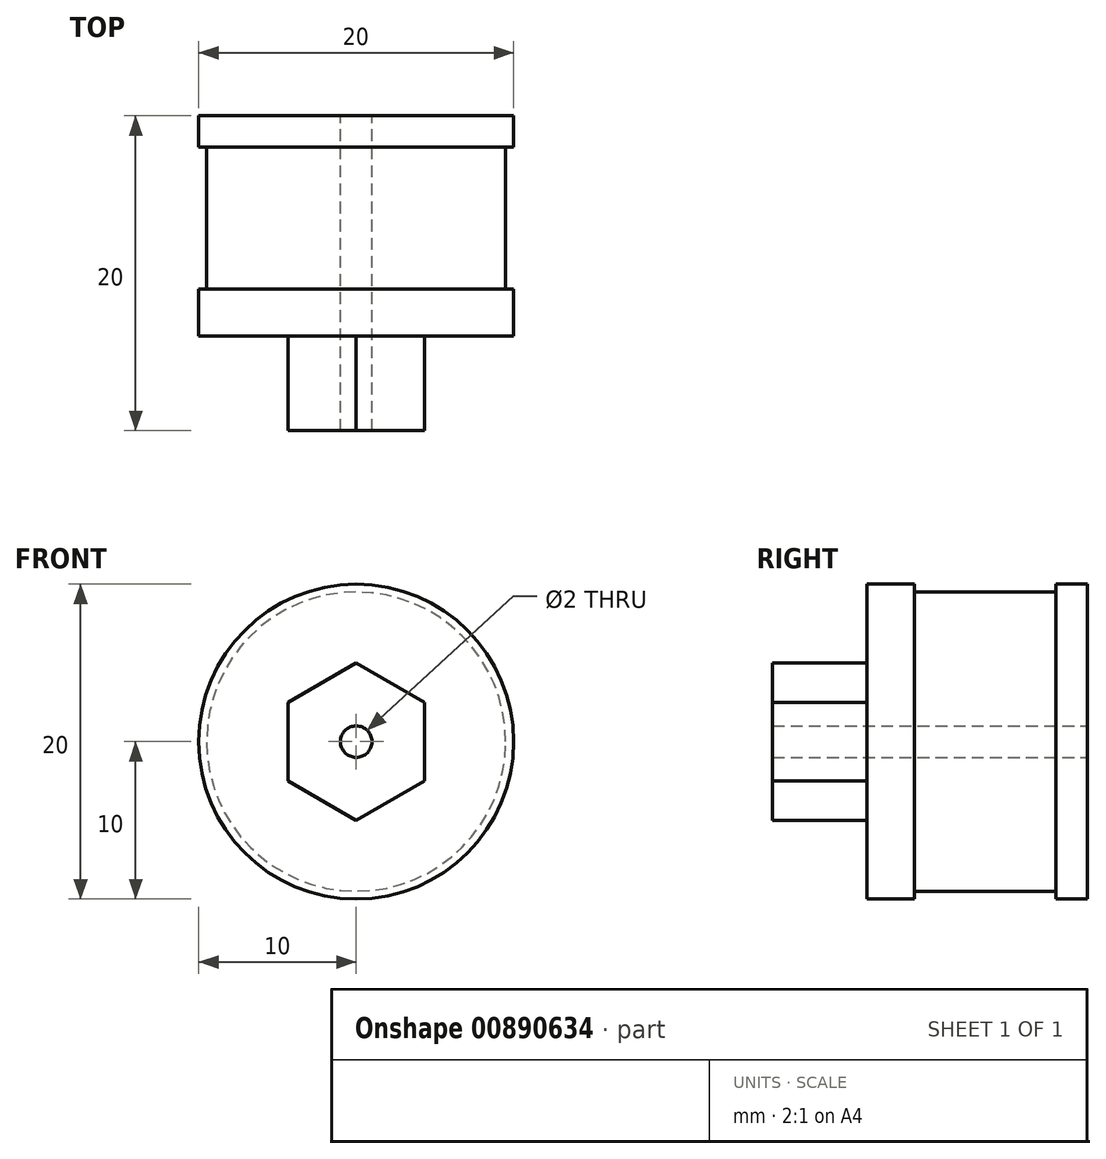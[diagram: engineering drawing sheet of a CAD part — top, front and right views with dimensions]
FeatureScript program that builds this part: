
annotation { "Feature Type Name" : "Feature", "Feature Type Description" : "" }
export const myFeature = defineFeature(function(context is Context, id is Id, definition is map)
    precondition{}
    {
        {
            var Q0;
            Q0=qCreatedBy(makeId("Front.planeOp"),FACE);
            var sketch = newSketch(context, id + "F0", { "sketchPlane" : qUnion([Q0])});
            skCircle(sketch, "E0", {"center": v(0, 0) * mm, "radius": 10 * mm});
            skCircle(sketch, "E1", {"center": v(0, 0) * mm, "radius": 5 * mm});
            skCircle(sketch, "E2", {"center": v(0, 0) * mm, "radius": 9.5 * mm});
            skCircle(sketch, "E3.cCircle", {"center": v(0, 0) * mm, "radius": 5 * mm, "construction": true});
            skLineSegment(sketch, "E3.0", {"start": v(0, 5) * mm, "end": v(4.33, 2.5) * mm});
            skLineSegment(sketch, "E3.1", {"start": v(4.33, 2.5) * mm, "end": v(4.33, -2.5) * mm});
            skLineSegment(sketch, "E3.2", {"start": v(4.33, -2.5) * mm, "end": v(0, -5) * mm});
            skLineSegment(sketch, "E3.3", {"start": v(0, -5) * mm, "end": v(-4.33, -2.5) * mm});
            skLineSegment(sketch, "E3.4", {"start": v(-4.33, -2.5) * mm, "end": v(-4.33, 2.5) * mm});
            skLineSegment(sketch, "E3.5", {"start": v(-4.33, 2.5) * mm, "end": v(0, 5) * mm});
            skCircle(sketch, "E4", {"center": v(0, 0) * mm, "radius": 1 * mm});
            skSolve(sketch);
        }
        {
            var Q0;
            Q0=makeQuery(id+"F0.imprint","IMPRINT",FACE,{"disambiguationData":[TD([[makeQuery(id+"F0.imprint","IMPRINT",EDGE,{"derivedFrom":sQuery(id+"F0.wireOp",EDGE,"E0")}),1.0]])]});
            var Q1;
            Q1=makeQuery(id+"F0.imprint","IMPRINT",FACE,{"disambiguationData":[TD([[makeQuery(id+"F0.imprint","IMPRINT",EDGE,{"derivedFrom":sQuery(id+"F0.wireOp",EDGE,"E2")}),1.0]])]});
            var Q2;
            {var subQ0=sQuery(id+"F0.wireOp",EDGE,"E3.0");Q2=makeQuery(id+"F0.imprint","IMPRINT",FACE,{"disambiguationData":[TD([[makeQuery(id+"F0.imprint","IMPRINT",EDGE,{"derivedFrom":subQ0}),1.0]])]});}
            var Q3;
            {var subQ0=sQuery(id+"F0.wireOp",EDGE,"E3.5");Q3=makeQuery(id+"F0.imprint","IMPRINT",FACE,{"disambiguationData":[TD([[makeQuery(id+"F0.imprint","IMPRINT",EDGE,{"derivedFrom":subQ0}),1.0]])]});}
            var Q4;
            {var subQ0=sQuery(id+"F0.wireOp",EDGE,"E3.4");Q4=makeQuery(id+"F0.imprint","IMPRINT",FACE,{"disambiguationData":[TD([[makeQuery(id+"F0.imprint","IMPRINT",EDGE,{"derivedFrom":subQ0}),1.0]])]});}
            var Q5;
            {var subQ0=sQuery(id+"F0.wireOp",EDGE,"E3.3");Q5=makeQuery(id+"F0.imprint","IMPRINT",FACE,{"disambiguationData":[TD([[makeQuery(id+"F0.imprint","IMPRINT",EDGE,{"derivedFrom":subQ0}),1.0]])]});}
            var Q6;
            {var subQ0=sQuery(id+"F0.wireOp",EDGE,"E3.2");Q6=makeQuery(id+"F0.imprint","IMPRINT",FACE,{"disambiguationData":[TD([[makeQuery(id+"F0.imprint","IMPRINT",EDGE,{"derivedFrom":subQ0}),1.0]])]});}
            var Q7;
            Q7=makeQuery(id+"F0.imprint","IMPRINT",FACE,{"disambiguationData":[TD([[makeQuery(id+"F0.imprint","IMPRINT",EDGE,{"derivedFrom":sQuery(id+"F0.wireOp",EDGE,"E3.0")}),-1.0]])]});
            var Q8;
            {var subQ0=sQuery(id+"F0.wireOp",EDGE,"E3.1");Q8=makeQuery(id+"F0.imprint","IMPRINT",FACE,{"disambiguationData":[TD([[makeQuery(id+"F0.imprint","IMPRINT",EDGE,{"derivedFrom":subQ0}),1.0]])]});}
            extrude(context, id + "F1", {"entities" : qUnion([Q0, Q1, Q2, Q3, Q4, Q5, Q6, Q7, Q8]), "depth" : 2 * mm, "offsetDistance" : 25 * mm});
        }
        {
            var Q0;
            {var subQ0=sQuery(id+"F0.wireOp",EDGE,"E3.5");Q0=makeQuery(id+"F0.imprint","IMPRINT",FACE,{"disambiguationData":[TD([[makeQuery(id+"F0.imprint","IMPRINT",EDGE,{"derivedFrom":subQ0}),1.0]])]});}
            var Q1;
            {var subQ0=sQuery(id+"F0.wireOp",EDGE,"E3.0");Q1=makeQuery(id+"F0.imprint","IMPRINT",FACE,{"disambiguationData":[TD([[makeQuery(id+"F0.imprint","IMPRINT",EDGE,{"derivedFrom":subQ0}),1.0]])]});}
            var Q2;
            Q2=makeQuery(id+"F0.imprint","IMPRINT",FACE,{"disambiguationData":[TD([[makeQuery(id+"F0.imprint","IMPRINT",EDGE,{"derivedFrom":sQuery(id+"F0.wireOp",EDGE,"E3.0")}),-1.0]])]});
            var Q3;
            {var subQ0=sQuery(id+"F0.wireOp",EDGE,"E3.1");Q3=makeQuery(id+"F0.imprint","IMPRINT",FACE,{"disambiguationData":[TD([[makeQuery(id+"F0.imprint","IMPRINT",EDGE,{"derivedFrom":subQ0}),1.0]])]});}
            var Q4;
            {var subQ0=sQuery(id+"F0.wireOp",EDGE,"E3.4");Q4=makeQuery(id+"F0.imprint","IMPRINT",FACE,{"disambiguationData":[TD([[makeQuery(id+"F0.imprint","IMPRINT",EDGE,{"derivedFrom":subQ0}),1.0]])]});}
            var Q5;
            {var subQ0=sQuery(id+"F0.wireOp",EDGE,"E3.3");Q5=makeQuery(id+"F0.imprint","IMPRINT",FACE,{"disambiguationData":[TD([[makeQuery(id+"F0.imprint","IMPRINT",EDGE,{"derivedFrom":subQ0}),1.0]])]});}
            var Q6;
            {var subQ0=sQuery(id+"F0.wireOp",EDGE,"E3.2");Q6=makeQuery(id+"F0.imprint","IMPRINT",FACE,{"disambiguationData":[TD([[makeQuery(id+"F0.imprint","IMPRINT",EDGE,{"derivedFrom":subQ0}),1.0]])]});}
            var Q7;
            Q7=makeQuery(id+"F0.imprint","IMPRINT",FACE,{"disambiguationData":[TD([[makeQuery(id+"F0.imprint","IMPRINT",EDGE,{"derivedFrom":sQuery(id+"F0.wireOp",EDGE,"E2")}),1.0]])]});
            extrude(context, id + "F2", {"entities" : qUnion([Q0, Q1, Q2, Q3, Q4, Q5, Q6, Q7]), "operationType" : NewBodyOperationType.ADD, "depth" : 12 * mm, "offsetDistance" : 25 * mm});
        }
        {
            var Q0;
            Q0=makeQuery(id+"F2.opExtrude","CAP_FACE",FACE,{"disambiguationData":[OSD([sQuery(id+"F0.wireOp",EDGE,"E2")])],"isStart":false});
            var sketch = newSketch(context, id + "F3", { "sketchPlane" : qUnion([Q0])});
            skCircle(sketch, "E5.0", {"center": v(0, 0) * mm, "radius": 10 * mm});
            skCircle(sketch, "E5.1", {"center": v(0, 0) * mm, "radius": 9.5 * mm});
            skCircle(sketch, "E5.2", {"center": v(0, 0) * mm, "radius": 5 * mm});
            skLineSegment(sketch, "E5.3", {"start": v(0, 5) * mm, "end": v(4.33, 2.5) * mm});
            skLineSegment(sketch, "E5.4", {"start": v(-4.33, 2.5) * mm, "end": v(0, 5) * mm});
            skLineSegment(sketch, "E5.5", {"start": v(0, -5) * mm, "end": v(-4.33, -2.5) * mm});
            skLineSegment(sketch, "E5.6", {"start": v(-4.33, -2.5) * mm, "end": v(-4.33, 2.5) * mm});
            skLineSegment(sketch, "E5.7", {"start": v(4.33, -2.5) * mm, "end": v(0, -5) * mm});
            skLineSegment(sketch, "E5.8", {"start": v(4.33, 2.5) * mm, "end": v(4.33, -2.5) * mm});
            skPoint(sketch, "E5.9", {"position": v(-2.17, 3.75) * mm});
            skPoint(sketch, "E5.10", {"position": v(2.17, 3.75) * mm});
            skPoint(sketch, "E5.11", {"position": v(-4.33, 0) * mm});
            skSolve(sketch);
        }
        {
            var Q0;
            Q0=makeQuery(id+"F3.imprint","IMPRINT",FACE,{"disambiguationData":[TD([[makeQuery(id+"F3.imprint","IMPRINT",EDGE,{"derivedFrom":sQuery(id+"F3.wireOp",EDGE,"E5.0")}),1.0]])]});
            var Q1;
            Q1=makeQuery(id+"F3.imprint","IMPRINT",FACE,{"disambiguationData":[TD([[makeQuery(id+"F3.imprint","IMPRINT",EDGE,{"derivedFrom":sQuery(id+"F3.wireOp",EDGE,"E5.1")}),1.0]])]});
            var Q2;
            {var subQ0=sQuery(id+"F3.wireOp",EDGE,"E5.4");Q2=makeQuery(id+"F3.imprint","IMPRINT",FACE,{"disambiguationData":[TD([[makeQuery(id+"F3.imprint","IMPRINT",EDGE,{"derivedFrom":subQ0}),1.0]])]});}
            var Q3;
            {var subQ0=sQuery(id+"F3.wireOp",EDGE,"E5.6");Q3=makeQuery(id+"F3.imprint","IMPRINT",FACE,{"disambiguationData":[TD([[makeQuery(id+"F3.imprint","IMPRINT",EDGE,{"derivedFrom":subQ0}),1.0]])]});}
            var Q4;
            {var subQ0=sQuery(id+"F3.wireOp",EDGE,"E5.3");Q4=makeQuery(id+"F3.imprint","IMPRINT",FACE,{"disambiguationData":[TD([[makeQuery(id+"F3.imprint","IMPRINT",EDGE,{"derivedFrom":subQ0}),1.0]])]});}
            var Q5;
            Q5=makeQuery(id+"F3.imprint","IMPRINT",FACE,{"disambiguationData":[TD([[makeQuery(id+"F3.imprint","IMPRINT",EDGE,{"derivedFrom":sQuery(id+"F3.wireOp",EDGE,"E5.3")}),-1.0]])]});
            var Q6;
            {var subQ0=sQuery(id+"F3.wireOp",EDGE,"E5.8");Q6=makeQuery(id+"F3.imprint","IMPRINT",FACE,{"disambiguationData":[TD([[makeQuery(id+"F3.imprint","IMPRINT",EDGE,{"derivedFrom":subQ0}),1.0]])]});}
            var Q7;
            {var subQ0=sQuery(id+"F3.wireOp",EDGE,"E5.7");Q7=makeQuery(id+"F3.imprint","IMPRINT",FACE,{"disambiguationData":[TD([[makeQuery(id+"F3.imprint","IMPRINT",EDGE,{"derivedFrom":subQ0}),1.0]])]});}
            var Q8;
            {var subQ0=sQuery(id+"F3.wireOp",EDGE,"E5.5");Q8=makeQuery(id+"F3.imprint","IMPRINT",FACE,{"disambiguationData":[TD([[makeQuery(id+"F3.imprint","IMPRINT",EDGE,{"derivedFrom":subQ0}),1.0]])]});}
            extrude(context, id + "F4", {"entities" : qUnion([Q0, Q1, Q2, Q3, Q4, Q5, Q6, Q7, Q8]), "depth" : 2 * mm, "offsetDistance" : 25 * mm});
        }
        {
            var Q0;
            Q0=makeQuery(id+"F3.imprint","IMPRINT",FACE,{"disambiguationData":[TD([[makeQuery(id+"F3.imprint","IMPRINT",EDGE,{"derivedFrom":sQuery(id+"F3.wireOp",EDGE,"E5.3")}),-1.0]])]});
            extrude(context, id + "F5", {"entities" : qUnion([Q0]), "operationType" : NewBodyOperationType.ADD, "depth" : 8 * mm, "offsetDistance" : 25 * mm});
        }
        {
            var Q0;
            Q0=makeQuery(id+"F3.imprint","IMPRINT",FACE,{"disambiguationData":[TD([[makeQuery(id+"F3.imprint","IMPRINT",EDGE,{"derivedFrom":makeQuery(id+"F2.opExtrude","CAP_EDGE",EDGE,{"disambiguationData":[OSD([sQuery(id+"F0.wireOp",EDGE,"E4")])],"isStart":false})}),1.0]])]});
            extrude(context, id + "F6", {"entities" : qUnion([Q0]), "operationType" : NewBodyOperationType.REMOVE, "depth" : 20 * mm, "offsetDistance" : 25 * mm});
        }
        {
            var Q0;
            Q0=makeQuery(id+"F3.imprint","IMPRINT",FACE,{"disambiguationData":[TD([[makeQuery(id+"F3.imprint","IMPRINT",EDGE,{"derivedFrom":sQuery(id+"F3.wireOp",EDGE,"E5.0")}),1.0]])]});
            extrude(context, id + "F7", {"entities" : qUnion([Q0]), "operationType" : NewBodyOperationType.ADD, "oppositeDirection" : true, "depth" : 1 * mm, "offsetDistance" : 25 * mm});
        }
    });
